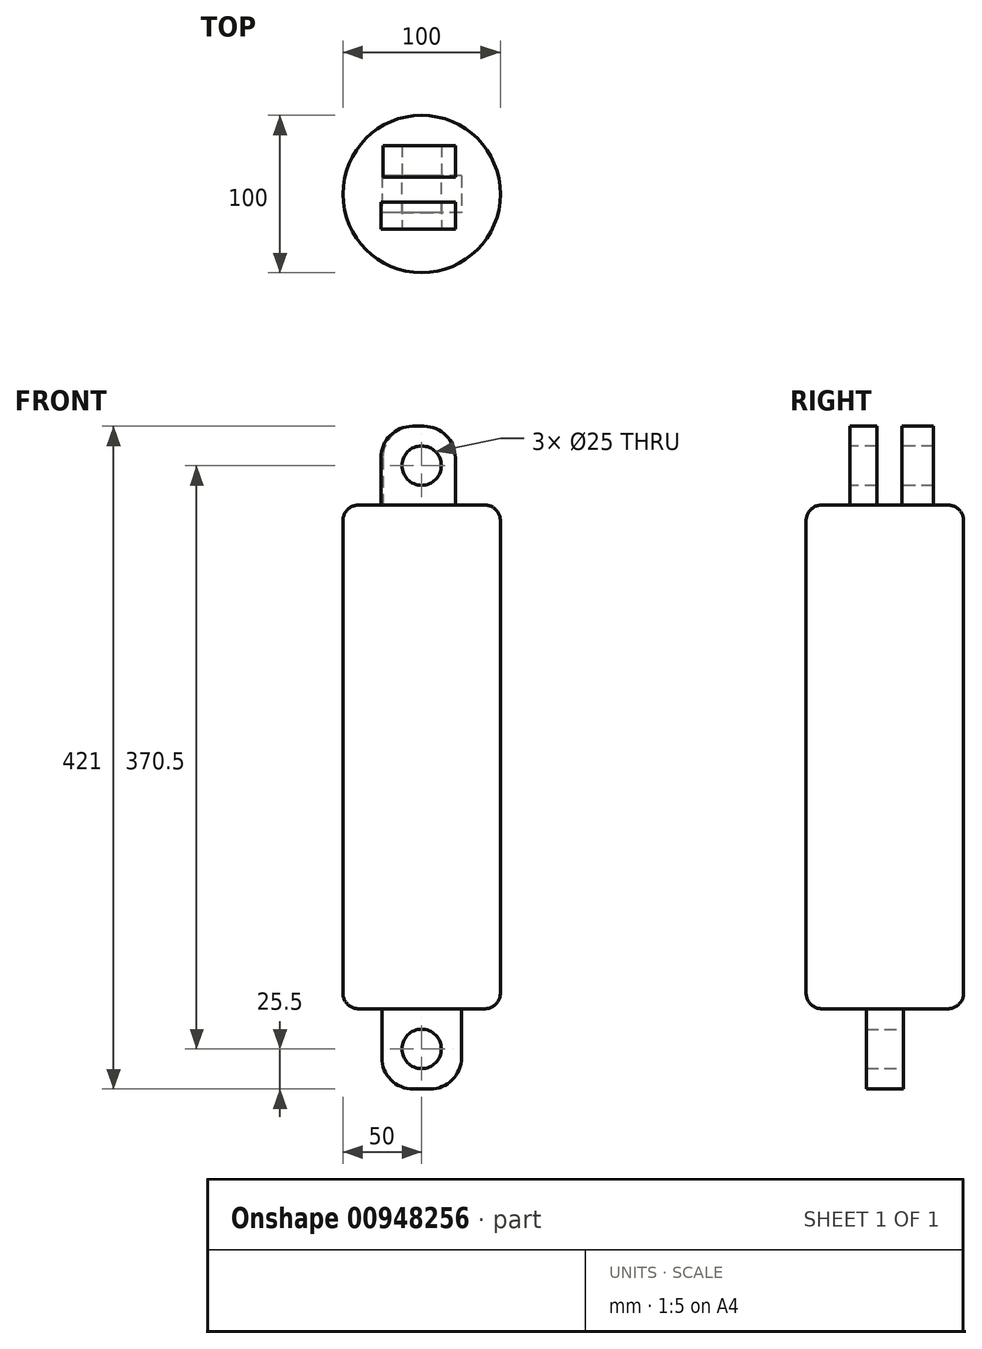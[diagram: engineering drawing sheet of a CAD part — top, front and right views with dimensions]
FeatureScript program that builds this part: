
annotation { "Feature Type Name" : "Feature", "Feature Type Description" : "" }
export const myFeature = defineFeature(function(context is Context, id is Id, definition is map)
    precondition{}
    {
        {
            var Q0;
            Q0=qCreatedBy(makeId("Top.planeOp"),FACE);
            var sketch = newSketch(context, id + "F0", { "sketchPlane" : qUnion([Q0])});
            skCircle(sketch, "E0", {"center": v(0, 0) * mm, "radius": 50 * mm});
            skSolve(sketch);
        }
        {
            var Q0;
            Q0=makeQuery(id+"F0.imprint","IMPRINT",FACE,{"disambiguationData":[TD([[makeQuery(id+"F0.imprint","IMPRINT",EDGE,{"derivedFrom":sQuery(id+"F0.wireOp",EDGE,"E0")}),1.0]])]});
            extrude(context, id + "F1", {"entities" : qUnion([Q0]), "depth" : 320 * mm, "offsetDistance" : 25 * mm});
        }
        {
            var Q0;
            Q0=makeQuery(id+"F1.opExtrude","CAP_FACE",FACE,{"disambiguationData":[OSD([sQuery(id+"F0.wireOp",EDGE,"E0")])],"isStart":false});
            var sketch = newSketch(context, id + "F2", { "sketchPlane" : qUnion([Q0])});
            skLineSegment(sketch, "E1.bottom", {"start": v(-25.85, -5.15) * mm, "end": v(21.4, -5.15) * mm});
            skLineSegment(sketch, "E1.top", {"start": v(-25.85, -22.14) * mm, "end": v(21.4, -22.14) * mm});
            skLineSegment(sketch, "E1.left", {"start": v(-25.85, -5.15) * mm, "end": v(-25.85, -22.14) * mm});
            skLineSegment(sketch, "E1.right", {"start": v(21.4, -5.15) * mm, "end": v(21.4, -22.14) * mm});
            skPoint(sketch, "E2.oppositeSnap0", {"position": v(21.4, -13.64) * mm});
            skLineSegment(sketch, "E2.bottom", {"start": v(-24.66, 10.75) * mm, "end": v(21.4, 10.75) * mm});
            skLineSegment(sketch, "E2.top", {"start": v(-24.66, 30.79) * mm, "end": v(21.4, 30.79) * mm});
            skLineSegment(sketch, "E2.left", {"start": v(-24.66, 10.75) * mm, "end": v(-24.66, 30.79) * mm});
            skLineSegment(sketch, "E2.right", {"start": v(21.4, 10.75) * mm, "end": v(21.4, 30.79) * mm});
            skSolve(sketch);
        }
        {
            var Q0;
            Q0=makeQuery(id+"F2.imprint","IMPRINT",FACE,{"disambiguationData":[TD([[makeQuery(id+"F2.imprint","IMPRINT",EDGE,{"derivedFrom":sQuery(id+"F2.wireOp",EDGE,"E1.bottom")}),-1.0]])]});
            var Q1;
            Q1=makeQuery(id+"F2.imprint","IMPRINT",FACE,{"disambiguationData":[TD([[makeQuery(id+"F2.imprint","IMPRINT",EDGE,{"derivedFrom":sQuery(id+"F2.wireOp",EDGE,"E2.bottom")}),1.0]])]});
            extrude(context, id + "F3", {"entities" : qUnion([Q0, Q1]), "operationType" : NewBodyOperationType.ADD, "depth" : 50 * mm, "offsetDistance" : 25 * mm});
        }
        {
            var Q0;
            Q0=makeQuery(id+"F3.opExtrude","SWEPT_FACE",FACE,{"disambiguationData":[OSD([sQuery(id+"F2.wireOp",EDGE,"E1.top")])]});
            var sketch = newSketch(context, id + "F4", { "sketchPlane" : qUnion([Q0])});
            skCircle(sketch, "E3", {"center": v(0, 345) * mm, "radius": 12.5 * mm});
            skPoint(sketch, "E4", {"position": v(21.4, 345) * mm});
            skSolve(sketch);
        }
        {
            var Q0;
            Q0=makeQuery(id+"F4.imprint","IMPRINT",FACE,{"disambiguationData":[TD([[makeQuery(id+"F4.imprint","IMPRINT",EDGE,{"derivedFrom":sQuery(id+"F4.wireOp",EDGE,"E3")}),1.0]])]});
            extrude(context, id + "F5", {"entities" : qUnion([Q0]), "operationType" : NewBodyOperationType.REMOVE, "endBound" : BoundingType.THROUGH_ALL, "oppositeDirection" : true, "depth" : 25 * mm, "offsetDistance" : 25 * mm});
        }
        {
            var Q0;
            Q0=qCreatedBy(makeId("Top.planeOp"),FACE);
            var sketch = newSketch(context, id + "F6", { "sketchPlane" : qUnion([Q0])});
            skLineSegment(sketch, "E5.bottom", {"start": v(25.3, 11.7) * mm, "end": v(-25.3, 11.7) * mm});
            skLineSegment(sketch, "E5.top", {"start": v(25.3, -11.7) * mm, "end": v(-25.3, -11.7) * mm});
            skLineSegment(sketch, "E5.left", {"start": v(25.3, 11.7) * mm, "end": v(25.3, -11.7) * mm});
            skLineSegment(sketch, "E5.right", {"start": v(-25.3, 11.7) * mm, "end": v(-25.3, -11.7) * mm});
            skPoint(sketch, "E5.middle", {"position": v(0, 0) * mm});
            skSolve(sketch);
        }
        {
            var Q0;
            Q0=makeQuery(id+"F6.imprint","IMPRINT",FACE,{"disambiguationData":[TD([[makeQuery(id+"F6.imprint","IMPRINT",EDGE,{"derivedFrom":sQuery(id+"F6.wireOp",EDGE,"E5.bottom")}),1.0]])]});
            extrude(context, id + "F7", {"entities" : qUnion([Q0]), "operationType" : NewBodyOperationType.ADD, "oppositeDirection" : true, "depth" : 51 * mm, "offsetDistance" : 25 * mm});
        }
        {
            var Q0;
            Q0=makeQuery(id+"F7.opExtrude","SWEPT_FACE",FACE,{"disambiguationData":[OSD([sQuery(id+"F6.wireOp",EDGE,"E5.bottom")])]});
            var sketch = newSketch(context, id + "F8", { "sketchPlane" : qUnion([Q0])});
            skCircle(sketch, "E6", {"center": v(0, -25.5) * mm, "radius": 12.5 * mm});
            skPoint(sketch, "E7", {"position": v(-25.3, -25.5) * mm});
            skSolve(sketch);
        }
        {
            var Q0;
            Q0=makeQuery(id+"F8.imprint","IMPRINT",FACE,{"disambiguationData":[TD([[makeQuery(id+"F8.imprint","IMPRINT",EDGE,{"derivedFrom":sQuery(id+"F8.wireOp",EDGE,"E6")}),1.0]])]});
            extrude(context, id + "F9", {"entities" : qUnion([Q0]), "operationType" : NewBodyOperationType.REMOVE, "endBound" : BoundingType.THROUGH_ALL, "oppositeDirection" : true, "depth" : 25 * mm, "offsetDistance" : 25 * mm});
        }
        {
            var Q0;
            Q0=makeQuery(id+"F3.opExtrude","CAP_EDGE",EDGE,{"disambiguationData":[OSD([sQuery(id+"F2.wireOp",EDGE,"E1.right")])],"isStart":false});
            var Q1;
            Q1=makeQuery(id+"F3.opExtrude","CAP_EDGE",EDGE,{"disambiguationData":[OSD([sQuery(id+"F2.wireOp",EDGE,"E2.right")])],"isStart":false});
            var Q2;
            Q2=makeQuery(id+"F3.opExtrude","CAP_EDGE",EDGE,{"disambiguationData":[OSD([sQuery(id+"F2.wireOp",EDGE,"E2.left")])],"isStart":false});
            var Q3;
            Q3=makeQuery(id+"F3.opExtrude","CAP_EDGE",EDGE,{"disambiguationData":[OSD([sQuery(id+"F2.wireOp",EDGE,"E1.left")])],"isStart":false});
            var Q4;
            Q4=makeQuery(id+"F7.opExtrude","CAP_EDGE",EDGE,{"disambiguationData":[OSD([sQuery(id+"F6.wireOp",EDGE,"E5.left")])],"isStart":false});
            var Q5;
            Q5=makeQuery(id+"F7.opExtrude","CAP_EDGE",EDGE,{"disambiguationData":[OSD([sQuery(id+"F6.wireOp",EDGE,"E5.right")])],"isStart":false});
            fillet(context, id + "F10", {"entities" : qUnion([Q0, Q1, Q2, Q3, Q4, Q5]), "radius" : 20 * mm, "tangentPropagation" : true, "allowEdgeOverflow" : false});
        }
        {
            var Q0;
            Q0=makeQuery(id+"F1.opExtrude","CAP_EDGE",EDGE,{"disambiguationData":[OSD([sQuery(id+"F0.wireOp",EDGE,"E0")])],"isStart":true});
            var Q1;
            Q1=makeQuery(id+"F1.opExtrude","CAP_EDGE",EDGE,{"disambiguationData":[OSD([sQuery(id+"F0.wireOp",EDGE,"E0")])],"isStart":false});
            fillet(context, id + "F11", {"entities" : qUnion([Q0, Q1]), "radius" : 10 * mm, "tangentPropagation" : true, "allowEdgeOverflow" : false});
        }
    });
